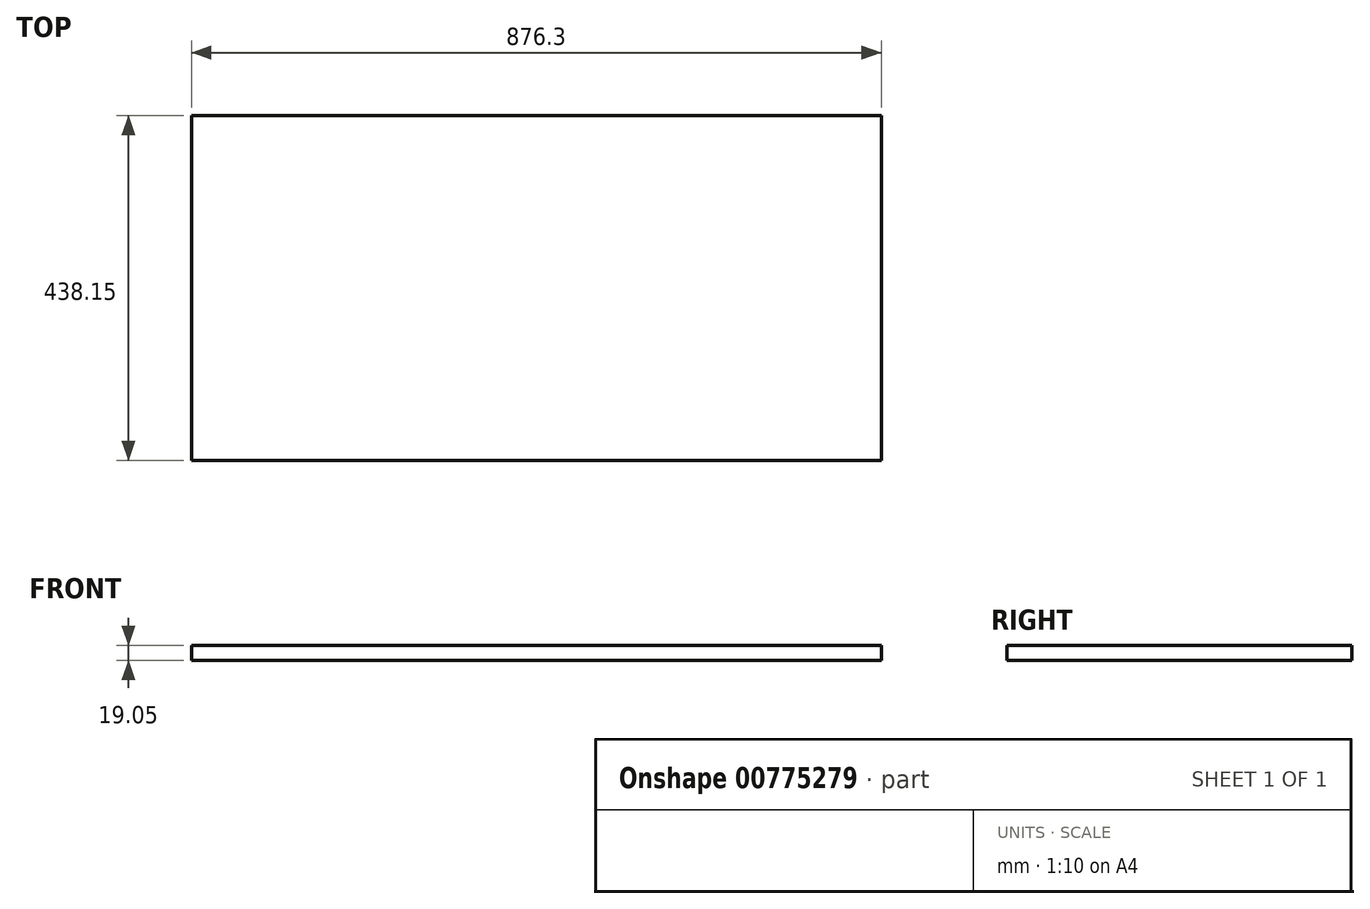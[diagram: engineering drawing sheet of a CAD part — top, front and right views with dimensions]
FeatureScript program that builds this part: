
annotation { "Feature Type Name" : "Feature", "Feature Type Description" : "" }
export const myFeature = defineFeature(function(context is Context, id is Id, definition is map)
    precondition{}
    {
        {
            var Q0;
            Q0=qCreatedBy(makeId("Top.planeOp"),FACE);
            var sketch = newSketch(context, id + "F0", { "sketchPlane" : qUnion([Q0])});
            skLineSegment(sketch, "E0.bottom", {"start": v(303.83, -208.4) * mm, "end": v(-572.47, -208.4) * mm});
            skLineSegment(sketch, "E0.top", {"start": v(303.83, 229.76) * mm, "end": v(-572.47, 229.76) * mm});
            skLineSegment(sketch, "E0.left", {"start": v(303.83, -208.4) * mm, "end": v(303.83, 229.76) * mm});
            skLineSegment(sketch, "E0.right", {"start": v(-572.47, -208.4) * mm, "end": v(-572.47, 229.76) * mm});
            skSolve(sketch);
        }
        {
            var Q0;
            Q0 = qSketchRegion(id + "F0", true);
            extrude(context, id + "F1", {"entities" : qUnion([Q0]), "depth" : 19.05 * mm, "offsetDistance" : 25.4 * mm});
        }
    });
